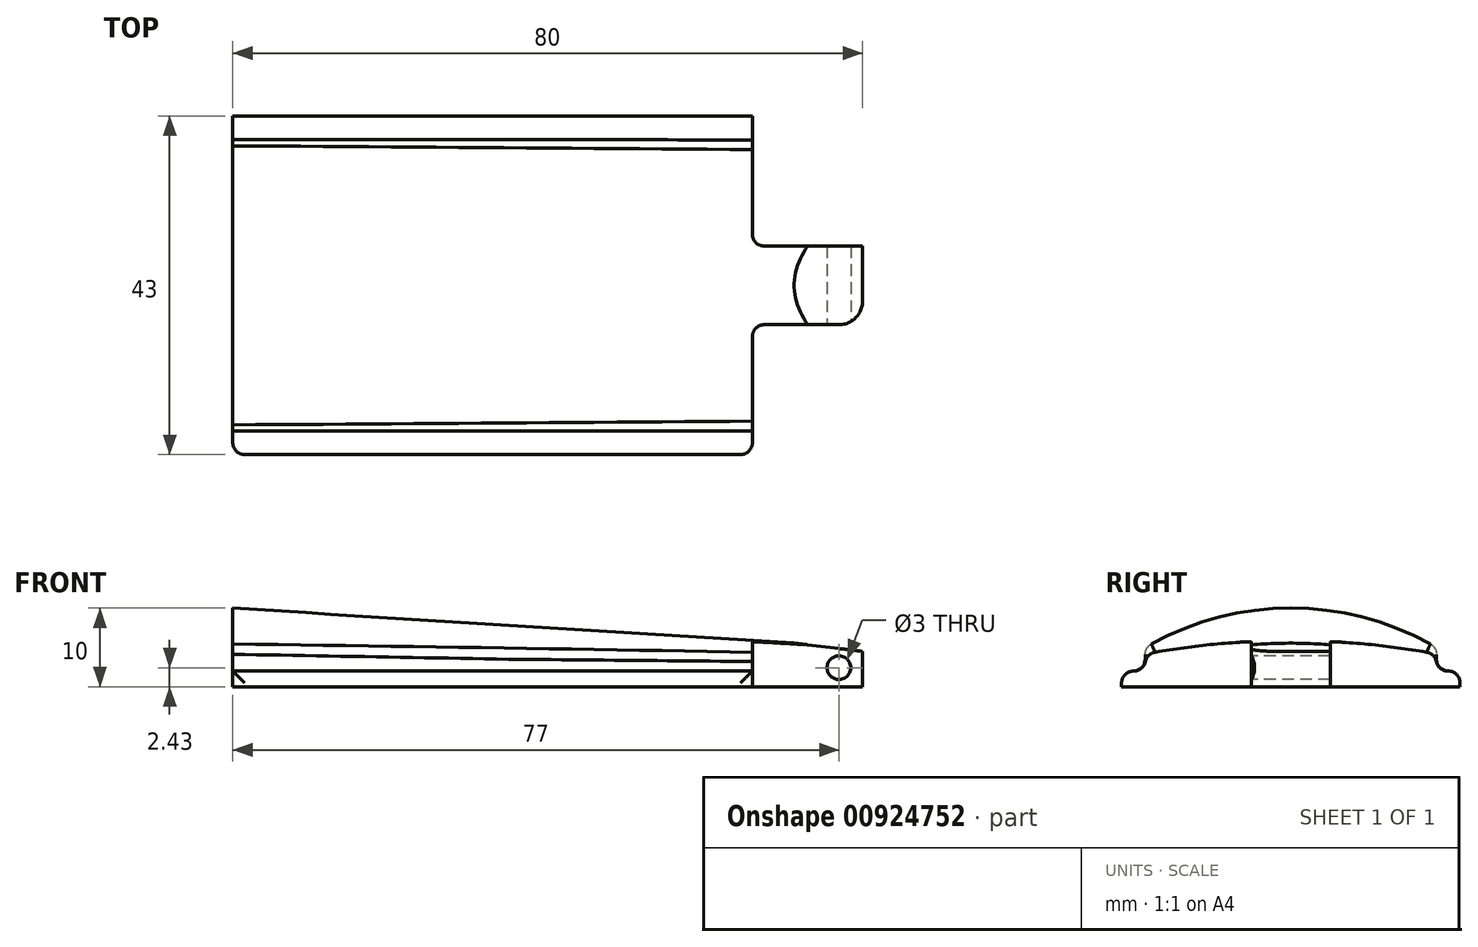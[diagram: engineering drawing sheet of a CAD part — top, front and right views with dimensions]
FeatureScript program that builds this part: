
annotation { "Feature Type Name" : "Feature", "Feature Type Description" : "" }
export const myFeature = defineFeature(function(context is Context, id is Id, definition is map)
    precondition{}
    {
        {
            var Q0;
            Q0=qCreatedBy(makeId("Right.planeOp"),FACE);
            cPlane(context, id + "F0", {"entities" : qUnion([Q0]), "cplaneType" : CPlaneType.OFFSET, "offset" : 80 * mm, "width" : 150 * mm, "height" : 150 * mm});
        }
        {
            var Q0;
            Q0=qCreatedBy(id+"F0.planeOp",FACE);
            var sketch = newSketch(context, id + "F1", { "sketchPlane" : qUnion([Q0])});
            skLineSegment(sketch, "E0", {"start": v(-21.5, 0) * mm, "end": v(21.5, 0) * mm});
            skLineSegment(sketch, "E1", {"start": v(21.5, 0) * mm, "end": v(21.5, 2) * mm});
            skLineSegment(sketch, "E2", {"start": v(21.5, 2) * mm, "end": v(18.5, 2) * mm});
            skLineSegment(sketch, "E3", {"start": v(18.5, 2) * mm, "end": v(18.5, 4) * mm});
            skLineSegment(sketch, "E4", {"start": v(-18.5, 4) * mm, "end": v(-18.5, 2) * mm});
            skLineSegment(sketch, "E5", {"start": v(-18.5, 2) * mm, "end": v(-21.5, 2) * mm});
            skLineSegment(sketch, "E6", {"start": v(-21.5, 2) * mm, "end": v(-21.5, 0) * mm});
            skArc(sketch, "E7", {"start": v(18.5, 4) * mm, "mid": v(0, 5) * mm, "end": v(-18.5, 4) * mm});
            skSolve(sketch);
        }
        {
            var Q0;
            Q0=qCreatedBy(makeId("Right.planeOp"),FACE);
            var sketch = newSketch(context, id + "F2", { "sketchPlane" : qUnion([Q0])});
            skLineSegment(sketch, "E8.0", {"start": v(-21.5, 0) * mm, "end": v(21.5, 0) * mm});
            skLineSegment(sketch, "E8.1", {"start": v(-21.5, 2) * mm, "end": v(-21.5, 0) * mm});
            skLineSegment(sketch, "E8.2", {"start": v(-18.5, 2) * mm, "end": v(-21.5, 2) * mm});
            skLineSegment(sketch, "E8.3", {"start": v(21.5, 0) * mm, "end": v(21.5, 2) * mm});
            skLineSegment(sketch, "E8.4", {"start": v(21.5, 2) * mm, "end": v(18.5, 2) * mm});
            skLineSegment(sketch, "E9", {"start": v(18.5, 2) * mm, "end": v(18.5, 5) * mm});
            skLineSegment(sketch, "E10", {"start": v(-18.5, 2) * mm, "end": v(-18.5, 5) * mm});
            skArc(sketch, "E11", {"start": v(18.5, 5) * mm, "mid": v(0, 10) * mm, "end": v(-18.5, 5) * mm});
            skSolve(sketch);
        }
        {
            var Q0;
            Q0=makeQuery(id+"F2.imprint","IMPRINT",FACE,{"disambiguationData":[TD([[makeQuery(id+"F2.imprint","IMPRINT",EDGE,{"derivedFrom":sQuery(id+"F2.wireOp",EDGE,"E8.0")}),1.0]])]});
            var Q1;
            Q1=makeQuery(id+"F1.imprint","IMPRINT",FACE,{"disambiguationData":[TD([[makeQuery(id+"F1.imprint","IMPRINT",EDGE,{"derivedFrom":sQuery(id+"F1.wireOp",EDGE,"E0")}),1.0]])]});
            loft(context, id + "F3", {"sheetProfilesArray" : [{ "sheetProfileEntities" : qUnion([Q0]) }, { "sheetProfileEntities" : qUnion([Q1]) }]});
        }
        {
            var Q0;
            Q0=makeQuery(id+"F3.opLoft","SWEPT_FACE",FACE,{"disambiguationData":[OSD([sQuery(id+"F1.wireOp",EDGE,"E0"),sQuery(id+"F1.wireOp",EDGE,"E1"),sQuery(id+"F1.wireOp",EDGE,"E6"),sQuery(id+"F2.wireOp",EDGE,"E8.0"),sQuery(id+"F2.wireOp",EDGE,"E8.1"),sQuery(id+"F2.wireOp",EDGE,"E8.3")])]});
            var sketch = newSketch(context, id + "F4", { "sketchPlane" : qUnion([Q0])});
            skPoint(sketch, "E12.orphan", {"position": v(80, 18.5) * mm});
            skPoint(sketch, "E13.orphan", {"position": v(80, -18.5) * mm});
            skLineSegment(sketch, "E14.bottom", {"start": v(80, 21.5) * mm, "end": v(66, 21.5) * mm});
            skLineSegment(sketch, "E14.top", {"start": v(80, 5) * mm, "end": v(66, 5) * mm});
            skLineSegment(sketch, "E14.left", {"start": v(80, 21.5) * mm, "end": v(80, 5) * mm});
            skLineSegment(sketch, "E14.right", {"start": v(66, 21.5) * mm, "end": v(66, 5) * mm});
            skLineSegment(sketch, "E15.bottom", {"start": v(80, -21.5) * mm, "end": v(66, -21.5) * mm});
            skLineSegment(sketch, "E15.top", {"start": v(80, -5) * mm, "end": v(66, -5) * mm});
            skLineSegment(sketch, "E15.left", {"start": v(80, -21.5) * mm, "end": v(80, -5) * mm});
            skLineSegment(sketch, "E15.right", {"start": v(66, -21.5) * mm, "end": v(66, -5) * mm});
            skSolve(sketch);
        }
        {
            var Q0;
            Q0 = qSketchRegion(id + "F4", true);
            extrude(context, id + "F5", {"entities" : qUnion([Q0]), "operationType" : NewBodyOperationType.REMOVE, "endBound" : BoundingType.THROUGH_ALL, "oppositeDirection" : true, "depth" : 25 * mm, "offsetDistance" : 25 * mm});
        }
        {
            var Q0;
            Q0=makeQuery(id+"F3.opLoft","SWEPT_EDGE",EDGE,{"disambiguationData":[OSD([sQuery(id+"F1.wireOp",EDGE,"E4"),sQuery(id+"F1.wireOp",EDGE,"E7"),sQuery(id+"F2.wireOp",EDGE,"E10"),sQuery(id+"F2.wireOp",EDGE,"E11")])]});
            var Q1;
            Q1=makeQuery(id+"F3.opLoft","SWEPT_EDGE",EDGE,{"disambiguationData":[OSD([sQuery(id+"F1.wireOp",EDGE,"E5"),sQuery(id+"F1.wireOp",EDGE,"E6"),sQuery(id+"F2.wireOp",EDGE,"E8.1"),sQuery(id+"F2.wireOp",EDGE,"E8.2")])]});
            var Q2;
            Q2=makeQuery(id+"F3.opLoft","SWEPT_EDGE",EDGE,{"disambiguationData":[OSD([sQuery(id+"F1.wireOp",EDGE,"E3"),sQuery(id+"F1.wireOp",EDGE,"E7"),sQuery(id+"F2.wireOp",EDGE,"E9"),sQuery(id+"F2.wireOp",EDGE,"E11")])]});
            var Q3;
            Q3=makeQuery(id+"F3.opLoft","SWEPT_EDGE",EDGE,{"disambiguationData":[OSD([sQuery(id+"F1.wireOp",EDGE,"E1"),sQuery(id+"F1.wireOp",EDGE,"E2"),sQuery(id+"F2.wireOp",EDGE,"E8.3"),sQuery(id+"F2.wireOp",EDGE,"E8.4")])]});
            var Q4;
            Q4=makeQuery(id+"F5.boolean.opBoolean","COPY",EDGE,{"derivedFrom":makeQuery(id+"F5.opExtrude","SWEPT_EDGE",EDGE,{"disambiguationData":[OSD([sQuery(id+"F4.wireOp",EDGE,"E14.top"),sQuery(id+"F4.wireOp",EDGE,"E14.right")])]})});
            var Q5;
            Q5=makeQuery(id+"F5.boolean.opBoolean","COPY",EDGE,{"derivedFrom":makeQuery(id+"F5.opExtrude","SWEPT_EDGE",EDGE,{"disambiguationData":[OSD([sQuery(id+"F4.wireOp",EDGE,"E15.top"),sQuery(id+"F4.wireOp",EDGE,"E15.right")])]})});
            fillet(context, id + "F6", {"entities" : qUnion([Q0, Q1, Q2, Q3, Q4, Q5]), "radius" : 1.5 * mm, "tangentPropagation" : true, "allowEdgeOverflow" : false});
        }
        {
            var Q0;
            Q0=makeQuery(id+"F3.opLoft","SWEPT_EDGE",EDGE,{"disambiguationData":[OSD([sQuery(id+"F1.wireOp",EDGE,"E4"),sQuery(id+"F1.wireOp",EDGE,"E5"),sQuery(id+"F2.wireOp",EDGE,"E8.2"),sQuery(id+"F2.wireOp",EDGE,"E10")])]});
            var Q1;
            Q1=makeQuery(id+"F3.opLoft","SWEPT_EDGE",EDGE,{"disambiguationData":[OSD([sQuery(id+"F1.wireOp",EDGE,"E2"),sQuery(id+"F1.wireOp",EDGE,"E3"),sQuery(id+"F2.wireOp",EDGE,"E8.4"),sQuery(id+"F2.wireOp",EDGE,"E9")])]});
            fillet(context, id + "F7", {"entities" : qUnion([Q0, Q1]), "radius" : 1.5 * mm, "tangentPropagation" : true, "allowEdgeOverflow" : false});
        }
        {
            var Q0;
            Q0=qCreatedBy(makeId("Front.planeOp"),FACE);
            var sketch = newSketch(context, id + "F8", { "sketchPlane" : qUnion([Q0])});
            skLineSegment(sketch, "E16", {"start": v(80, 4.5) * mm, "end": v(70, 5.7) * mm});
            skLineSegment(sketch, "E17", {"start": v(70, 5.7) * mm, "end": v(80, 5.7) * mm});
            skLineSegment(sketch, "E18", {"start": v(80, 5.7) * mm, "end": v(80, 4.5) * mm});
            skSolve(sketch);
        }
        {
            var Q0;
            Q0 = qSketchRegion(id + "F8", true);
            extrude(context, id + "F9", {"entities" : qUnion([Q0]), "operationType" : NewBodyOperationType.REMOVE, "endBound" : BoundingType.THROUGH_ALL, "oppositeDirection" : true, "depth" : 25 * mm, "offsetDistance" : 25 * mm, "hasSecondDirection" : true, "secondDirectionBound" : BoundingType.THROUGH_ALL, "secondDirectionOppositeDirection" : false, "secondDirectionDepth" : 25 * mm});
        }
        {
            var Q0;
            Q0=makeQuery(id+"F3.opLoft","SWEPT_FACE",FACE,{"disambiguationData":[OSD([sQuery(id+"F1.wireOp",EDGE,"E0"),sQuery(id+"F1.wireOp",EDGE,"E1"),sQuery(id+"F1.wireOp",EDGE,"E6"),sQuery(id+"F2.wireOp",EDGE,"E8.0"),sQuery(id+"F2.wireOp",EDGE,"E8.1"),sQuery(id+"F2.wireOp",EDGE,"E8.3")])]});
            var sketch = newSketch(context, id + "F10", { "sketchPlane" : qUnion([Q0])});
            skArc(sketch, "E19", {"start": v(1.5, 21.5) * mm, "mid": v(0.44, 21.06) * mm, "end": v(0, 20) * mm});
            skLineSegment(sketch, "E20", {"start": v(0, 20) * mm, "end": v(0, 21.5) * mm});
            skLineSegment(sketch, "E21", {"start": v(0, 21.5) * mm, "end": v(1.5, 21.5) * mm});
            skLineSegment(sketch, "E22", {"start": v(64.5, 21.5) * mm, "end": v(66, 21.5) * mm});
            skLineSegment(sketch, "E23", {"start": v(66, 21.5) * mm, "end": v(66, 20) * mm});
            skArc(sketch, "E24", {"start": v(66, 20) * mm, "mid": v(65.56, 21.06) * mm, "end": v(64.5, 21.5) * mm});
            skLineSegment(sketch, "E25", {"start": v(77, 5) * mm, "end": v(80, 5) * mm});
            skLineSegment(sketch, "E26", {"start": v(80, 5) * mm, "end": v(80, 2) * mm});
            skArc(sketch, "E27", {"start": v(80, 2) * mm, "mid": v(79.12, 4.12) * mm, "end": v(77, 5) * mm});
            skSolve(sketch);
        }
        {
            var Q0;
            Q0 = qSketchRegion(id + "F10", true);
            extrude(context, id + "F11", {"entities" : qUnion([Q0]), "operationType" : NewBodyOperationType.REMOVE, "endBound" : BoundingType.THROUGH_ALL, "oppositeDirection" : true, "depth" : 25 * mm, "offsetDistance" : 25 * mm});
        }
        {
            var Q0;
            Q0=qCreatedBy(makeId("Front.planeOp"),FACE);
            var sketch = newSketch(context, id + "F12", { "sketchPlane" : qUnion([Q0])});
            skCircle(sketch, "E28", {"center": v(77, 2.43) * mm, "radius": 1.5 * mm});
            skLineSegment(sketch, "E29.0", {"start": v(77, 4.86) * mm, "end": v(77, 0) * mm, "construction": true});
            skSolve(sketch);
        }
        {
            var Q0;
            Q0 = qSketchRegion(id + "F12", true);
            extrude(context, id + "F13", {"entities" : qUnion([Q0]), "operationType" : NewBodyOperationType.REMOVE, "endBound" : BoundingType.THROUGH_ALL, "oppositeDirection" : true, "depth" : 25 * mm, "offsetDistance" : 25 * mm, "hasSecondDirection" : true, "secondDirectionBound" : BoundingType.THROUGH_ALL, "secondDirectionOppositeDirection" : false, "secondDirectionDepth" : 25 * mm});
        }
    });
